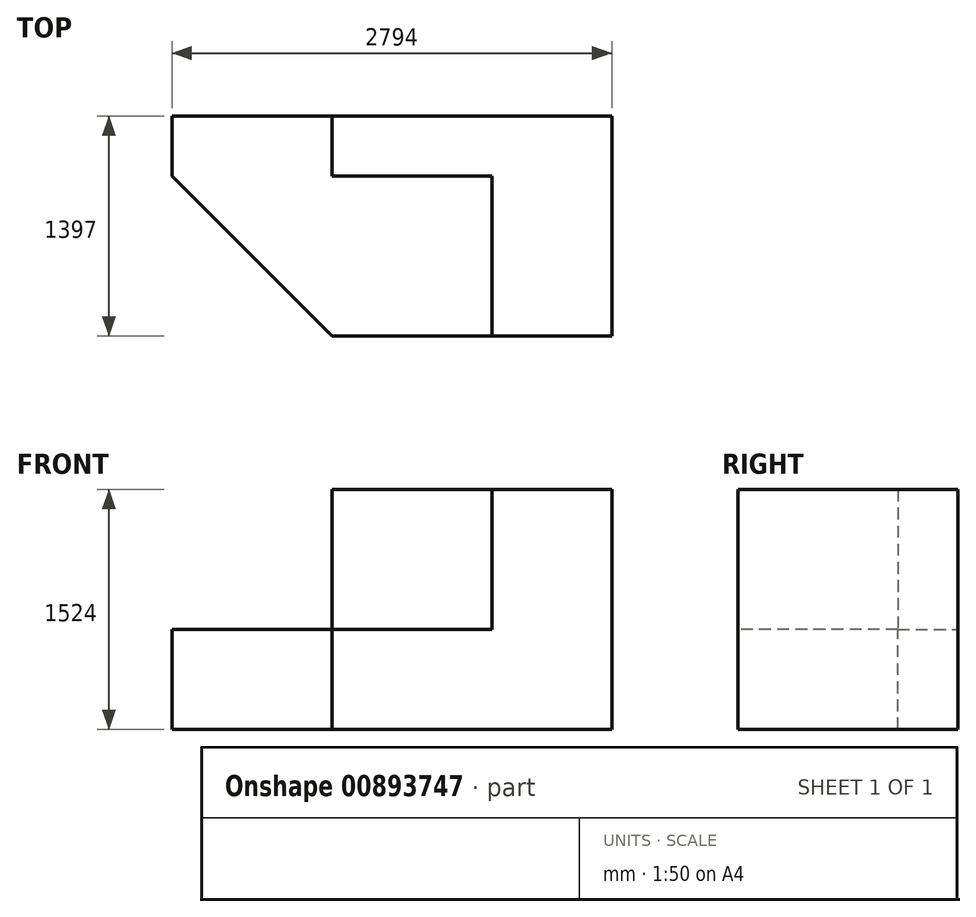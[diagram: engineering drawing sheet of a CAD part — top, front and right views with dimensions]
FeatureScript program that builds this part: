
annotation { "Feature Type Name" : "Feature", "Feature Type Description" : "" }
export const myFeature = defineFeature(function(context is Context, id is Id, definition is map)
    precondition{}
    {
        {
            var Q0;
            Q0=qCreatedBy(makeId("Front.planeOp"),FACE);
            var sketch = newSketch(context, id + "F0", { "sketchPlane" : qUnion([Q0])});
            skLineSegment(sketch, "E0.bottom", {"start": v(-155.15, -87.16) * mm, "end": v(2638.85, -87.16) * mm});
            skLineSegment(sketch, "E0.top", {"start": v(-155.15, 547.84) * mm, "end": v(2638.85, 547.84) * mm});
            skLineSegment(sketch, "E0.left", {"start": v(-155.15, -87.16) * mm, "end": v(-155.15, 547.84) * mm});
            skLineSegment(sketch, "E0.right", {"start": v(2638.85, -87.16) * mm, "end": v(2638.85, 547.84) * mm});
            skSolve(sketch);
        }
        {
            var Q0;
            Q0=makeQuery(id+"F0.imprint","IMPRINT",FACE,{"disambiguationData":[TD([[makeQuery(id+"F0.imprint","IMPRINT",EDGE,{"derivedFrom":sQuery(id+"F0.wireOp",EDGE,"E0.bottom")}),1.0]])]});
            extrude(context, id + "F1", {"entities" : qUnion([Q0]), "depth" : 1397 * mm, "offsetDistance" : 25.4 * mm});
        }
        {
            var Q0;
            Q0=makeQuery(id+"F1.opExtrude","SWEPT_FACE",FACE,{"disambiguationData":[OSD([sQuery(id+"F0.wireOp",EDGE,"E0.top")])]});
            var sketch = newSketch(context, id + "F2", { "sketchPlane" : qUnion([Q0])});
            skLineSegment(sketch, "E1.bottom", {"start": v(2638.85, 0) * mm, "end": v(1876.85, 0) * mm});
            skLineSegment(sketch, "E1.top", {"start": v(2638.85, -1397) * mm, "end": v(1876.85, -1397) * mm});
            skLineSegment(sketch, "E1.left", {"start": v(2638.85, 0) * mm, "end": v(2638.85, -1397) * mm});
            skLineSegment(sketch, "E1.right", {"start": v(1876.85, 0) * mm, "end": v(1876.85, -1397) * mm});
            skSolve(sketch);
        }
        {
            var Q0;
            Q0=makeQuery(id+"F2.imprint","IMPRINT",FACE,{"disambiguationData":[TD([[makeQuery(id+"F2.imprint","IMPRINT",EDGE,{"derivedFrom":sQuery(id+"F2.wireOp",EDGE,"E1.bottom")}),-1.0]])]});
            extrude(context, id + "F3", {"entities" : qUnion([Q0]), "operationType" : NewBodyOperationType.ADD, "depth" : 889 * mm, "offsetDistance" : 25.4 * mm});
        }
        {
            var Q0;
            Q0=makeQuery(id+"F1.opExtrude","SWEPT_FACE",FACE,{"disambiguationData":[OSD([sQuery(id+"F0.wireOp",EDGE,"E0.top")])]});
            var sketch = newSketch(context, id + "F4", { "sketchPlane" : qUnion([Q0])});
            skLineSegment(sketch, "E2.bottom", {"start": v(1876.85, 0) * mm, "end": v(860.85, 0) * mm});
            skLineSegment(sketch, "E2.top", {"start": v(1876.85, -381) * mm, "end": v(860.85, -381) * mm});
            skLineSegment(sketch, "E2.left", {"start": v(1876.85, 0) * mm, "end": v(1876.85, -381) * mm});
            skLineSegment(sketch, "E2.right", {"start": v(860.85, 0) * mm, "end": v(860.85, -381) * mm});
            skSolve(sketch);
        }
        {
            var Q0;
            Q0=makeQuery(id+"F4.imprint","IMPRINT",FACE,{"disambiguationData":[TD([[makeQuery(id+"F4.imprint","IMPRINT",EDGE,{"derivedFrom":sQuery(id+"F4.wireOp",EDGE,"E2.bottom")}),-1.0]])]});
            extrude(context, id + "F5", {"entities" : qUnion([Q0]), "operationType" : NewBodyOperationType.ADD, "depth" : 889 * mm, "offsetDistance" : 25.4 * mm});
        }
        {
            var Q0;
            Q0=makeQuery(id+"F1.opExtrude","SWEPT_FACE",FACE,{"disambiguationData":[OSD([sQuery(id+"F0.wireOp",EDGE,"E0.top")])]});
            var sketch = newSketch(context, id + "F6", { "sketchPlane" : qUnion([Q0])});
            skLineSegment(sketch, "E3", {"start": v(860.85, -1397) * mm, "end": v(860.85, -381) * mm});
            skLineSegment(sketch, "E4", {"start": v(860.85, -381) * mm, "end": v(-155.15, -381) * mm});
            skLineSegment(sketch, "E5", {"start": v(-155.15, -381) * mm, "end": v(860.85, -1397) * mm});
            skSolve(sketch);
        }
        {
            var Q0;
            {var subQ0=sQuery(id+"F6.wireOp",EDGE,"E5");Q0=makeQuery(id+"F6.imprint","IMPRINT",FACE,{"disambiguationData":[TD([[makeQuery(id+"F6.imprint","IMPRINT",EDGE,{"derivedFrom":subQ0}),-1.0]])]});}
            extrude(context, id + "F7", {"entities" : qUnion([Q0]), "operationType" : NewBodyOperationType.REMOVE, "oppositeDirection" : true, "depth" : 2194.56 * mm, "offsetDistance" : 25.4 * mm});
        }
    });
